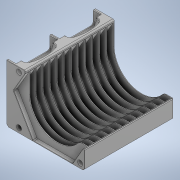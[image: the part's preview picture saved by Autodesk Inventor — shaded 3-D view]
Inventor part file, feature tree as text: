
AUTODESK INVENTOR PART (.ipt)
format: ipt  version: 2021 (Build 250183000, 183)  size: 790,016 bytes
history: native  units: mm
features: extrude x8, sketch x7, projected_geometry x7, fillet x3, chamfer x3, pattern_linear x2, plane x2, other x2, loft x1, mirror x1
ambient origin geometry x8: Origin, YZ Plane, XZ Plane, XY Plane, X Axis, Y Axis, Z Axis, Center Point
bodies: Solid1 (feature_tree)
feature tree (36):
  extrude  "Extrusion1"  Depth=0.25mm
  fillet  "Fillet1"  Radius=0.25mm
  extrude  "Extrusion2"  Depth=1.0mm
  pattern_linear  "Rectangular Pattern1"  Count1=3  [1 undecoded]
  pattern_linear  "Rectangular Pattern2"  Count1=13  [1 undecoded]
  extrude  "Extrusion3"  Depth=1.0mm
  chamfer  "Chamfer1"  Distance=2.0mm
  chamfer  "Chamfer2"  Distance=13.0mm
  chamfer  "Chamfer3"  Distance=23.0mm
  plane  "Work Plane1"
  sketch  "Sketch4"  dims[d9=125.0mm d10=30.0mm d11=130.0mm]
  extrude  "Extrusion4"  Depth=1.0mm
  extrude  "Extrusion5"  Depth=1.0mm
  extrude  "Extrusion6"  Depth=1.0mm
  extrude  "Extrusion7"  Depth=1.0mm
  extrude  "Extrusion8"  Depth=1.0mm
  plane  "Work Plane2"
  loft  "Loft1"
  fillet  "Fillet2"  Radius=30.0mm
  fillet  "Fillet3"  Radius=142.5mm
  mirror  "Mirror1"
  sketch  "Sketch1"  dims[d0=108.4mm d1=0.25mm d2=0.25mm]
  sketch  "Sketch2"  dims[d4=1.0mm d5=0.25mm]
  projected_geometry  "Projected Loop1"
  sketch  "Sketch3"  dims[d6=11.126556mm]
  projected_geometry  "Projected Loop2"
  projected_geometry  "Projected Loop3"
  projected_geometry  "Projected Loop4"
  projected_geometry  "Projected Loop5"
  sketch  "Sketch5"  dims[d12=1.0mm d13=36.0mm]
  projected_geometry  "Projected Loop6"
  sketch  "Sketch6"  dims[d14=1.0mm]
  projected_geometry  "Projected Loop7"
  sketch  "Sketch7"  dims[d15=32.0mm d16=2.0mm d17=13.0mm d18=23.0mm d19=2.98813mm d20=92.0mm d21=106.0mm d22=38.0mm d23=32.373046mm d24=21.24649mm d25=30.0mm d26=142.5mm d27=0.0mm d28=10.0mm d29=1.2mm d30=0.0mm d31=120.0mm d33=11.344mm d34=20.0mm d36=134.628mm d37=54.0mm d38=44.0mm d39=8.0mm d40=30.0mm d41=8.0mm d42=6.0mm d43=0.0mm d44=2.0mm d45=3.0mm d46=2.0mm d47=45.0deg d48=0.75mm d49=2.0mm d50=45.0deg d51=0.5mm d52=2.0mm d53=45.0deg d54=-1.5mm d55=65.0mm d56=88.0mm d57=3.5mm d58=1.0mm d60=0.5mm d61=0.5mm d62=2.0mm d63=3.5mm d64=1.75mm d65=0.0mm d66=0.0mm d67=9.0mm d68=0.0mm d69=10.5mm d70=0.0mm d71=2.0mm d72=50.0mm d73=10.5mm d74=32.0mm d75=1.0mm d76=0.0mm d77=2.0mm d78=8.0mm d79=65.0mm d80=1.0mm d81=0.0mm d82=7.0mm d83=0.0mm d84=90.0deg d85=0.0mm d86=90.0deg d87=0.0mm d88=90.0deg d89=5.0mm d90=1.0mm d91=2.0mm d92=1.0mm d93=74.0mm d94=20.0mm]
  other  "Edges1"
  other  "Edges2"
note: 2 required parameter values undecoded (feature->parameter linkage not recoverable at this tier; creation-order binding heuristic only, values carry confidence <= 0.55)
